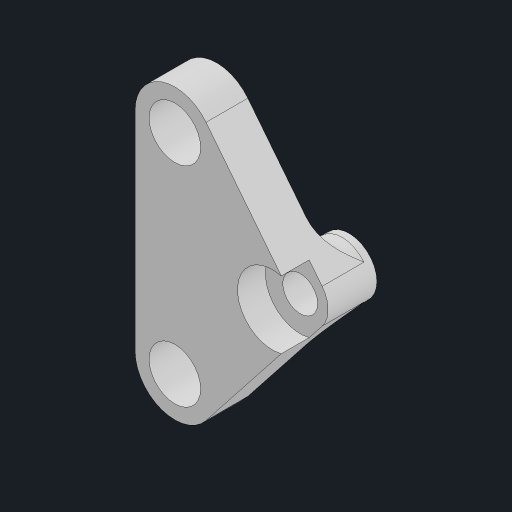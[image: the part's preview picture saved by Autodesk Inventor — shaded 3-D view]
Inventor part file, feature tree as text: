
AUTODESK INVENTOR PART (.ipt)
format: ipt  version: 2023.2 (Build 272271030, 271C)  size: 334,848 bytes
history: native  units: mm
features: extrude x3, sketch x3, fillet x1, projected_geometry x1
ambient origin geometry x8: Origin, YZ Plane, XZ Plane, XY Plane, X Axis, Y Axis, Z Axis, Center Point
bodies: Solid1 (feature_tree)
feature tree (8):
  extrude  "Extrusion1"  Depth=4.0mm
  extrude  "Extrusion3"  Depth=5.5mm
  fillet  "Fillet2"  Radius=7.0mm
  extrude  "Extrusion4"  Depth=2.0mm
  sketch  "Sketch1"  dims[d0=2.5mm d1=4.0mm]
  sketch  "Sketch3"  dims[d2=5.5mm d3=0.0mm d9=3.7mm d10=7.0mm]
  projected_geometry  "Projected Loop1"
  sketch  "Sketch4"  dims[d11=15.0mm d12=7.5mm d13=5.7mm d14=3.0mm d15=0.0mm d16=2.0mm d17=5.0mm d18=2.0mm d19=0.0mm]
